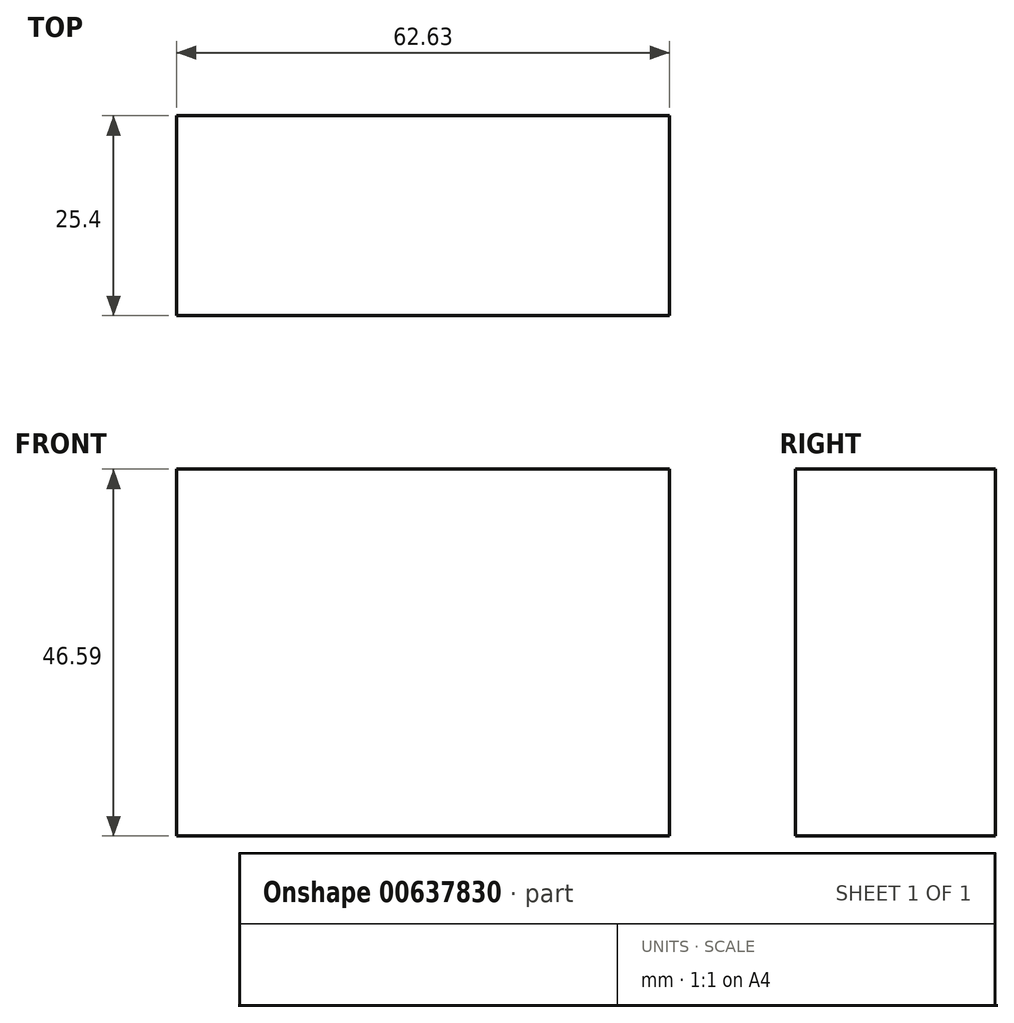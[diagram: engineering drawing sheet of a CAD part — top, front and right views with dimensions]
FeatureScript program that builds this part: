
annotation { "Feature Type Name" : "Feature", "Feature Type Description" : "" }
export const myFeature = defineFeature(function(context is Context, id is Id, definition is map)
    precondition{}
    {
        {
            var Q0;
            Q0=qCreatedBy(makeId("Front.planeOp"),FACE);
            var sketch = newSketch(context, id + "F0", { "sketchPlane" : qUnion([Q0])});
            skLineSegment(sketch, "E0.bottom", {"start": v(-35.61, 24.92) * mm, "end": v(27.02, 24.92) * mm});
            skLineSegment(sketch, "E0.top", {"start": v(-35.61, -21.67) * mm, "end": v(27.02, -21.67) * mm});
            skLineSegment(sketch, "E0.left", {"start": v(-35.61, 24.92) * mm, "end": v(-35.61, -21.67) * mm});
            skLineSegment(sketch, "E0.right", {"start": v(27.02, 24.92) * mm, "end": v(27.02, -21.67) * mm});
            skSolve(sketch);
        }
        {
            var Q0;
            Q0 = qSketchRegion(id + "F0", true);
            extrude(context, id + "F1", {"entities" : qUnion([Q0]), "depth" : 25.4 * mm, "offsetDistance" : 25.4 * mm});
        }
    });
